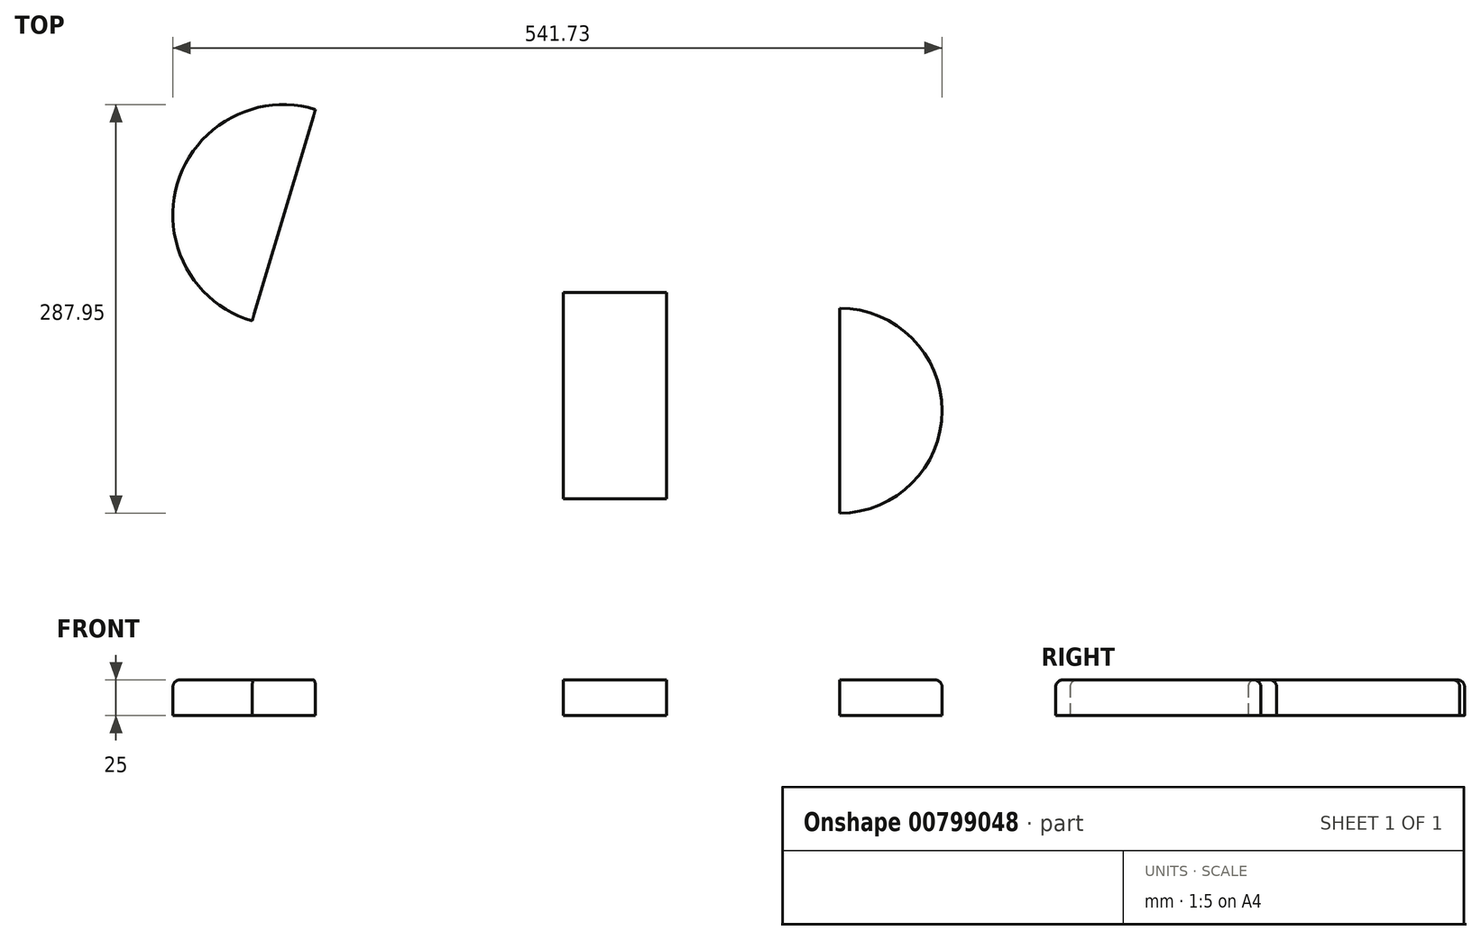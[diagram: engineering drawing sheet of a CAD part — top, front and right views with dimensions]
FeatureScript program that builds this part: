
annotation { "Feature Type Name" : "Feature", "Feature Type Description" : "" }
export const myFeature = defineFeature(function(context is Context, id is Id, definition is map)
    precondition{}
    {
        {
            var Q0;
            Q0=qCreatedBy(makeId("Top.planeOp"),FACE);
            var sketch = newSketch(context, id + "F0", { "sketchPlane" : qUnion([Q0])});
            skLineSegment(sketch, "E0", {"start": v(0, -79.53) * mm, "end": v(0, 65.01) * mm});
            skLineSegment(sketch, "E1", {"start": v(0, 65.01) * mm, "end": v(0, 65.01) * mm});
            skArc(sketch, "E2", {"start": v(0, -79.53) * mm, "mid": v(72.27, -7.26) * mm, "end": v(0, 65.01) * mm});
            skSolve(sketch);
        }
        {
            var Q0;
            Q0=makeQuery(id+"F0.imprint","IMPRINT",FACE,{"disambiguationData":[TD([[makeQuery(id+"F0.imprint","IMPRINT",EDGE,{"derivedFrom":sQuery(id+"F0.wireOp",EDGE,"E0")}),-1.0]])]});
            extrude(context, id + "F1", {"entities" : qUnion([Q0]), "depth" : 25 * mm, "offsetDistance" : 25 * mm});
        }
        {
            var Q0;
            Q0=qCreatedBy(makeId("Top.planeOp"),FACE);
            var sketch = newSketch(context, id + "F2", { "sketchPlane" : qUnion([Q0])});
            skLineSegment(sketch, "E3.bottom", {"start": v(-121.9, -69.46) * mm, "end": v(-194.4, -69.46) * mm});
            skLineSegment(sketch, "E3.top", {"start": v(-121.9, 76.1) * mm, "end": v(-194.4, 76.1) * mm});
            skLineSegment(sketch, "E3.left", {"start": v(-121.9, -69.46) * mm, "end": v(-121.9, 76.1) * mm});
            skLineSegment(sketch, "E3.right", {"start": v(-194.4, -69.46) * mm, "end": v(-194.4, 76.1) * mm});
            skSolve(sketch);
        }
        {
            var Q0;
            Q0=makeQuery(id+"F2.imprint","IMPRINT",FACE,{"disambiguationData":[TD([[makeQuery(id+"F2.imprint","IMPRINT",EDGE,{"derivedFrom":sQuery(id+"F2.wireOp",EDGE,"E3.bottom")}),-1.0]])]});
            extrude(context, id + "F3", {"entities" : qUnion([Q0]), "depth" : 25 * mm, "offsetDistance" : 25 * mm});
        }
        {
            var Q0;
            Q0=makeQuery(id+"F3.opExtrude","CAP_EDGE",EDGE,{"disambiguationData":[OSD([sQuery(id+"F2.wireOp",EDGE,"E3.bottom")])],"isStart":false});
            var Q1;
            Q1=makeQuery(id+"F3.opExtrude","CAP_EDGE",EDGE,{"disambiguationData":[OSD([sQuery(id+"F2.wireOp",EDGE,"E3.top")])],"isStart":false});
            fillet(context, id + "F4", {"entities" : qUnion([Q0, Q1]), "radius" : 5 * mm, "tangentPropagation" : true, "allowEdgeOverflow" : false});
        }
        {
            var Q0;
            Q0=makeQuery(id+"F1.opExtrude","CAP_EDGE",EDGE,{"disambiguationData":[OSD([sQuery(id+"F0.wireOp",EDGE,"E2")])],"isStart":false});
            fillet(context, id + "F5", {"entities" : qUnion([Q0]), "radius" : 5 * mm, "tangentPropagation" : true, "allowEdgeOverflow" : false});
        }
        {
            var Q0;
            Q0=qCreatedBy(makeId("Top.planeOp"),FACE);
            var sketch = newSketch(context, id + "F6", { "sketchPlane" : qUnion([Q0])});
            skLineSegment(sketch, "E4", {"start": v(-413.61, 55.9) * mm, "end": v(-368.99, 205.05) * mm});
            skArc(sketch, "E5", {"start": v(-368.99, 205.05) * mm, "mid": v(-466.2, 152.89) * mm, "end": v(-413.61, 55.9) * mm});
            skSolve(sketch);
        }
        {
            var Q0;
            Q0 = qSketchRegion(id + "F6", true);
            extrude(context, id + "F7", {"entities" : qUnion([Q0]), "depth" : 25 * mm, "offsetDistance" : 25 * mm});
        }
        {
            var Q0;
            Q0=makeQuery(id+"F7.opExtrude","CAP_EDGE",EDGE,{"disambiguationData":[OSD([sQuery(id+"F6.wireOp",EDGE,"E5")])],"isStart":false});
            fillet(context, id + "F8", {"entities" : qUnion([Q0]), "radius" : 5 * mm, "tangentPropagation" : true, "allowEdgeOverflow" : false});
        }
    });
